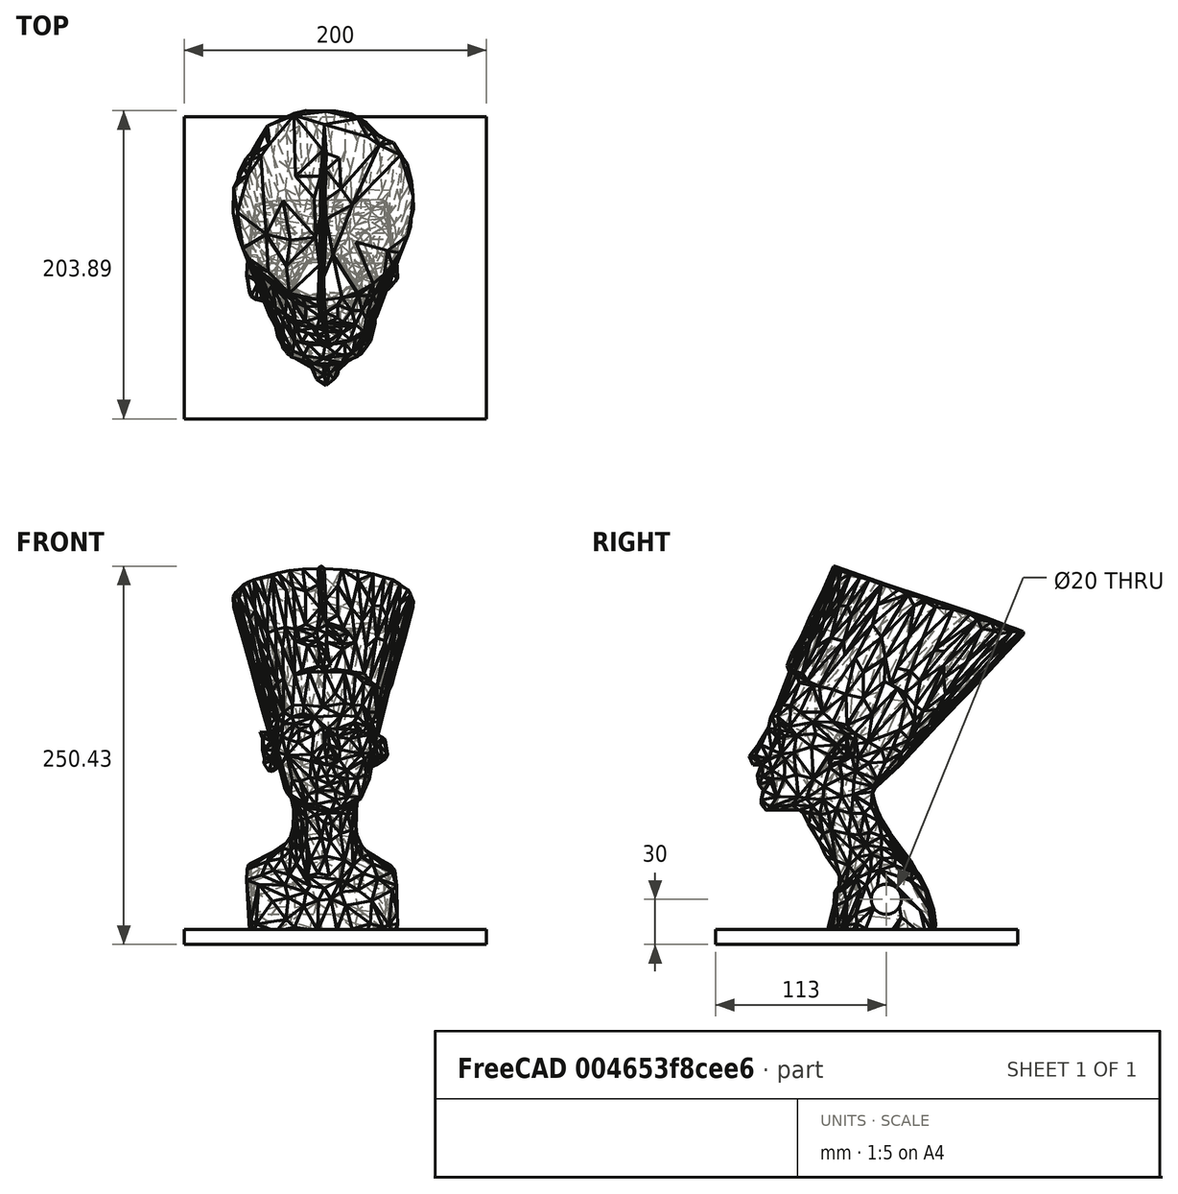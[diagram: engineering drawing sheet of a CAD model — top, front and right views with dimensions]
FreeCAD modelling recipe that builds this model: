
FCSTD DOCUMENT  (FreeCAD 0.17R13217 (Git))
Label: 02-nefertiti-peana
License: All rights reserved
LicenseURL: http://en.wikipedia.org/wiki/All_rights_reserved
objects: Part::Feature×3, Mesh::Feature×1, Part::Box×1, Part::MultiFuse×1, Part::Cylinder×1, Part::Cut×1
note: 7 computed .brp shape members not serialized (recipe doc carries the construction recipe); baked Part::Feature solids carry a one-line shape summary decoded from their .brp

FEATURE [Mesh::Feature] _1_Lowpoly_Nefertiti  label="01-Lowpoly-Nefertiti"
FEATURE [Part::Feature] _1_Lowpoly_Nefertiti001
  shape: bbox 119.3 x 181.8 x 245.4 mm, 1540 faces, 0 solids (baked)
FEATURE [Part::Feature] _1_Lowpoly_Nefertiti001001  label="_1_Lowpoly_Nefertiti002"
  shape: bbox 119.3 x 181.8 x 245.4 mm, 1491 faces, 0 solids (baked)
FEATURE [Part::Feature] _1_Lowpoly_Nefertiti001001_solid  label="_1_Lowpoly_Nefertiti002 (Solid)"
  shape: bbox 119.3 x 181.8 x 245.4 mm, 1491 faces (baked)
FEATURE [Part::Box] Box  label="Cubo"
  AttacherType = Attacher::AttachEngine3D
  Height = 10
  Length = 200
  Placement = pos=(-92,-113,-3) rot=(0,0,1;0rad)
  Width = 200
FEATURE [Part::MultiFuse] Fusion
  Refine = true
  Shapes = -> [_1_Lowpoly_Nefertiti001001_solid,Box]
FEATURE [Part::Cylinder] Cylinder  label="Cilindro"
  Angle = 360
  AttacherType = Attacher::AttachEngine3D
  Height = 300
  Placement = pos=(-135,0,27) rot=(0,1,0;1.5708rad)
  Radius = 10
FEATURE [Part::Cut] Cut
  Base = -> Fusion
  Refine = true
  Tool = -> Cylinder
